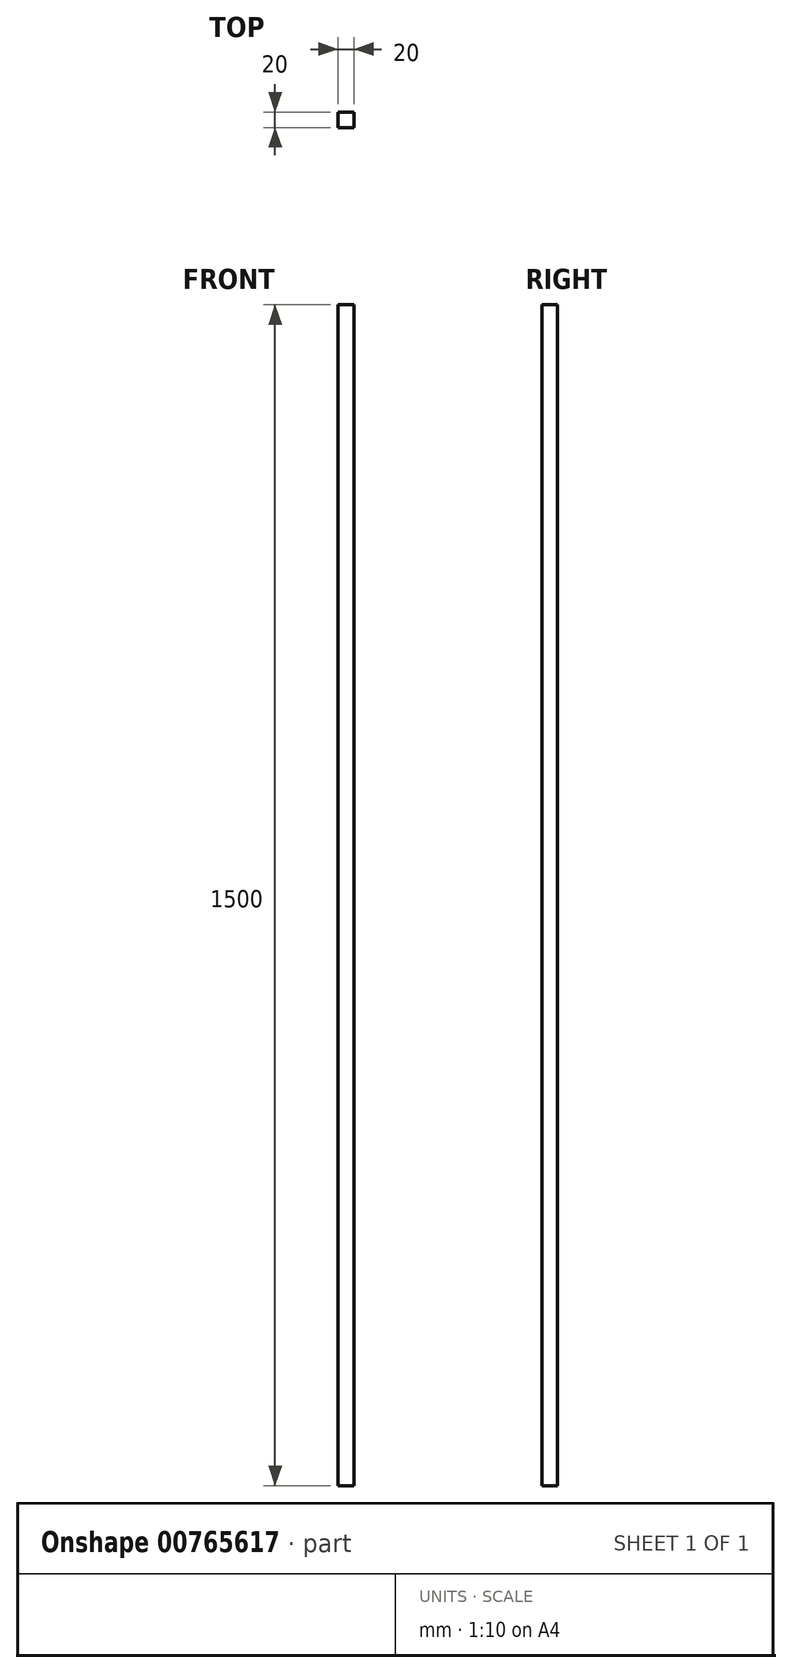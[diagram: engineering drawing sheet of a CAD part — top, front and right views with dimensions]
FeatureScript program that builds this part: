
annotation { "Feature Type Name" : "Feature", "Feature Type Description" : "" }
export const myFeature = defineFeature(function(context is Context, id is Id, definition is map)
    precondition{}
    {
        {
            var Q0;
            Q0=qCreatedBy(makeId("Top.planeOp"),FACE);
            var sketch = newSketch(context, id + "F0", { "sketchPlane" : qUnion([Q0])});
            skLineSegment(sketch, "E0.bottom", {"start": v(10, -10) * mm, "end": v(-10, -10) * mm});
            skLineSegment(sketch, "E0.top", {"start": v(10, 10) * mm, "end": v(-10, 10) * mm});
            skLineSegment(sketch, "E0.left", {"start": v(10, -10) * mm, "end": v(10, 10) * mm});
            skLineSegment(sketch, "E0.right", {"start": v(-10, -10) * mm, "end": v(-10, 10) * mm});
            skPoint(sketch, "E0.middle", {"position": v(0, 0) * mm});
            skSolve(sketch);
        }
        {
            var Q0;
            Q0 = qSketchRegion(id + "F0", true);
            extrude(context, id + "F1", {"entities" : qUnion([Q0]), "depth" : 1500 * mm, "offsetDistance" : 25 * mm});
        }
    });
